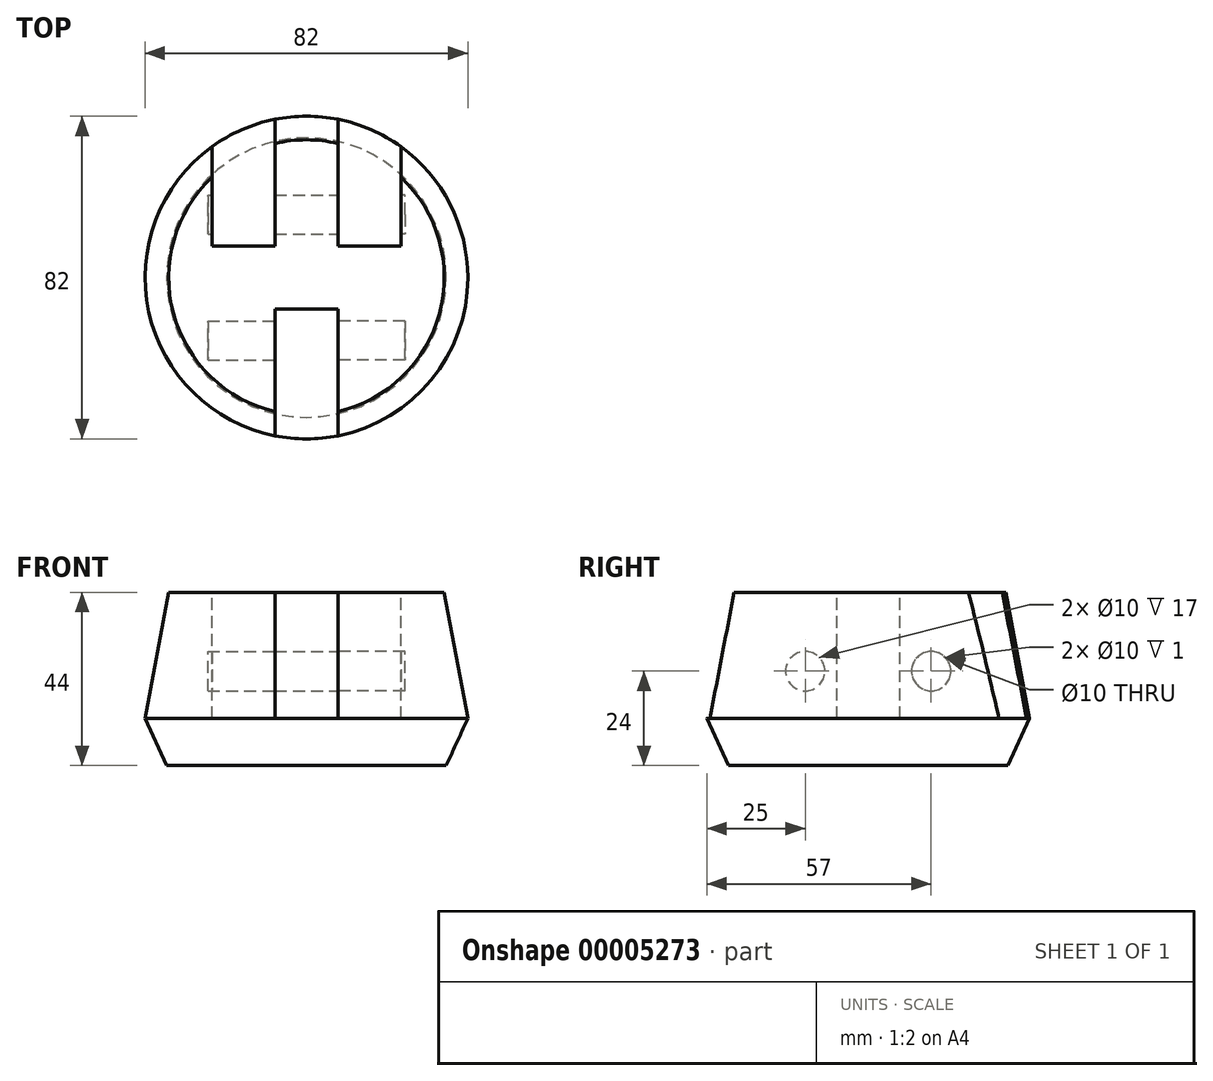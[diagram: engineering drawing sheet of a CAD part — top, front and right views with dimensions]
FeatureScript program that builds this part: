
annotation { "Feature Type Name" : "Feature", "Feature Type Description" : "" }
export const myFeature = defineFeature(function(context is Context, id is Id, definition is map)
    precondition{}
    {
        {
            var Q0;
            Q0=qCreatedBy(makeId("Top.planeOp"),FACE);
            var sketch = newSketch(context, id + "F0", { "sketchPlane" : qUnion([Q0])});
            skCircle(sketch, "E0", {"center": v(0, 0) * mm, "radius": 35.5 * mm});
            skSolve(sketch);
        }
        {
            var Q0;
            Q0=qCreatedBy(makeId("Top.planeOp"),FACE);
            cPlane(context, id + "F1", {"entities" : qUnion([Q0]), "cplaneType" : CPlaneType.OFFSET, "offset" : 12 * mm, "width" : 150 * mm, "height" : 150 * mm});
        }
        {
            var Q0;
            Q0=qCreatedBy(id+"F1.planeOp",FACE);
            cPlane(context, id + "F2", {"entities" : qUnion([Q0]), "cplaneType" : CPlaneType.OFFSET, "offset" : 32 * mm, "width" : 150 * mm, "height" : 150 * mm});
        }
        {
            var Q0;
            Q0=qCreatedBy(id+"F1.planeOp",FACE);
            var sketch = newSketch(context, id + "F3", { "sketchPlane" : qUnion([Q0])});
            skCircle(sketch, "E1", {"center": v(0, 0) * mm, "radius": 41 * mm});
            skSolve(sketch);
        }
        {
            var Q0;
            Q0=qCreatedBy(id+"F2.planeOp",FACE);
            var sketch = newSketch(context, id + "F4", { "sketchPlane" : qUnion([Q0])});
            skCircle(sketch, "E2", {"center": v(0, 0) * mm, "radius": 35 * mm});
            skSolve(sketch);
        }
        {
            var Q0;
            Q0=makeQuery(id+"F0.imprint","IMPRINT",FACE,{"disambiguationData":[TD([[makeQuery(id+"F0.imprint","IMPRINT",EDGE,{"derivedFrom":sQuery(id+"F0.wireOp",EDGE,"E0")}),1.0]])]});
            var Q1;
            Q1=makeQuery(id+"F3.imprint","IMPRINT",FACE,{"disambiguationData":[TD([[makeQuery(id+"F3.imprint","IMPRINT",EDGE,{"derivedFrom":sQuery(id+"F3.wireOp",EDGE,"E1")}),1.0]])]});
            loft(context, id + "F5", {"sheetProfilesArray" : [{ "sheetProfileEntities" : qUnion([Q0]) }, { "sheetProfileEntities" : qUnion([Q1]) }]});
        }
        {
            var Q1;
            Q1=makeQuery(id+"F3.imprint","IMPRINT",FACE,{"disambiguationData":[TD([[makeQuery(id+"F3.imprint","IMPRINT",EDGE,{"derivedFrom":sQuery(id+"F3.wireOp",EDGE,"E1")}),1.0]])]});
            var Q2;
            Q2=makeQuery(id+"F4.imprint","IMPRINT",FACE,{"disambiguationData":[TD([[makeQuery(id+"F4.imprint","IMPRINT",EDGE,{"derivedFrom":sQuery(id+"F4.wireOp",EDGE,"E2")}),1.0]])]});
            loft(context, id + "F6", {"operationType" : NewBodyOperationType.ADD, "sheetProfilesArray" : [{ "sheetProfileEntities" : qUnion([Q1]) }, { "sheetProfileEntities" : qUnion([Q2]) }]});
        }
        {
            var Q0;
            Q0=makeQuery(id+"F6.opLoft","CAP_FACE",FACE,{"disambiguationData":[OSD([makeQuery(id+"F4.imprint","IMPRINT",FACE,{"disambiguationData":[TD([[makeQuery(id+"F4.imprint","IMPRINT",EDGE,{"derivedFrom":sQuery(id+"F4.wireOp",EDGE,"E2")}),1.0]])]})])],"isStart":true});
            var sketch = newSketch(context, id + "F7", { "sketchPlane" : qUnion([Q0])});
            skLineSegment(sketch, "E3.bottom", {"start": v(-8, -48) * mm, "end": v(8, -48) * mm});
            skLineSegment(sketch, "E3.top", {"start": v(-8, -8) * mm, "end": v(8, -8) * mm});
            skLineSegment(sketch, "E3.left", {"start": v(-8, -48) * mm, "end": v(-8, -8) * mm});
            skLineSegment(sketch, "E3.right", {"start": v(8, -48) * mm, "end": v(8, -8) * mm});
            skLineSegment(sketch, "E4.bottom", {"start": v(-24, 48) * mm, "end": v(-8, 48) * mm});
            skLineSegment(sketch, "E4.top", {"start": v(-24, 8) * mm, "end": v(-8, 8) * mm});
            skLineSegment(sketch, "E4.left", {"start": v(-24, 48) * mm, "end": v(-24, 8) * mm});
            skLineSegment(sketch, "E4.right", {"start": v(-8, 48) * mm, "end": v(-8, 8) * mm});
            skLineSegment(sketch, "E5.bottom", {"start": v(8, 48) * mm, "end": v(24, 48) * mm});
            skLineSegment(sketch, "E5.top", {"start": v(8, 8) * mm, "end": v(24, 8) * mm});
            skLineSegment(sketch, "E5.left", {"start": v(8, 48) * mm, "end": v(8, 8) * mm});
            skLineSegment(sketch, "E5.right", {"start": v(24, 48) * mm, "end": v(24, 8) * mm});
            skPoint(sketch, "E6", {"position": v(0, -8) * mm});
            skSolve(sketch);
        }
        {
            var Q0;
            {var subQ6=sQuery(id+"F7.wireOp",EDGE,"E3.bottom");var subQ12=sQuery(id+"F7.wireOp",EDGE,"E4.bottom");var subQ18=sQuery(id+"F7.wireOp",EDGE,"E5.bottom");var subQ19=sQuery(id+"F7.wireOp",EDGE,"E3.top");var subQ20=sQuery(id+"F7.wireOp",EDGE,"E4.top");var subQ21=sQuery(id+"F7.wireOp",EDGE,"E5.top");Q0=qUnion([makeQuery(id+"F7.imprint","IMPRINT",FACE,{"disambiguationData":[TD([[makeQuery(id+"F7.imprint","IMPRINT",EDGE,{"derivedFrom":subQ6}),1.0]])]}),makeQuery(id+"F7.imprint","IMPRINT",FACE,{"disambiguationData":[TD([[makeQuery(id+"F7.imprint","IMPRINT",EDGE,{"derivedFrom":subQ12}),-1.0]])]}),makeQuery(id+"F7.imprint","IMPRINT",FACE,{"disambiguationData":[TD([[makeQuery(id+"F7.imprint","IMPRINT",EDGE,{"derivedFrom":subQ18}),-1.0]])]}),makeQuery(id+"F7.imprint","IMPRINT",FACE,{"disambiguationData":[TD([[makeQuery(id+"F7.imprint","IMPRINT",EDGE,{"derivedFrom":subQ19}),-1.0]])]}),makeQuery(id+"F7.imprint","IMPRINT",FACE,{"disambiguationData":[TD([[makeQuery(id+"F7.imprint","IMPRINT",EDGE,{"derivedFrom":subQ20}),1.0]])]}),makeQuery(id+"F7.imprint","IMPRINT",FACE,{"disambiguationData":[TD([[makeQuery(id+"F7.imprint","IMPRINT",EDGE,{"derivedFrom":subQ21}),1.0]])]})]);}
            extrude(context, id + "F8", {"entities" : qUnion([Q0]), "operationType" : NewBodyOperationType.REMOVE, "oppositeDirection" : true, "depth" : 32 * mm});
        }
        {
            var Q0;
            Q0=qCreatedBy(makeId("Right.planeOp"),FACE);
            var sketch = newSketch(context, id + "F9", { "sketchPlane" : qUnion([Q0])});
            skCircle(sketch, "E7", {"center": v(-16, 24) * mm, "radius": 5 * mm});
            skCircle(sketch, "E8", {"center": v(16, 24) * mm, "radius": 5 * mm});
            skSolve(sketch);
        }
        {
            var Q0;
            {Q0=qUnion([makeQuery(id+"F9.imprint","IMPRINT",FACE,{"disambiguationData":[TD([[makeQuery(id+"F9.imprint","IMPRINT",EDGE,{"derivedFrom":sQuery(id+"F9.wireOp",EDGE,"E7")}),1.0]])]}),makeQuery(id+"F9.imprint","IMPRINT",FACE,{"disambiguationData":[TD([[makeQuery(id+"F9.imprint","IMPRINT",EDGE,{"derivedFrom":sQuery(id+"F9.wireOp",EDGE,"E8")}),1.0]])]})]);}
            extrude(context, id + "F10", {"entities" : qUnion([Q0]), "operationType" : NewBodyOperationType.REMOVE, "oppositeDirection" : true, "depth" : 25 * mm});
        }
        {
            var Q0;
            {Q0=qUnion([makeQuery(id+"F9.imprint","IMPRINT",FACE,{"disambiguationData":[TD([[makeQuery(id+"F9.imprint","IMPRINT",EDGE,{"derivedFrom":sQuery(id+"F9.wireOp",EDGE,"E7")}),1.0]])]}),makeQuery(id+"F9.imprint","IMPRINT",FACE,{"disambiguationData":[TD([[makeQuery(id+"F9.imprint","IMPRINT",EDGE,{"derivedFrom":sQuery(id+"F9.wireOp",EDGE,"E8")}),1.0]])]})]);}
            extrude(context, id + "F11", {"entities" : qUnion([Q0]), "operationType" : NewBodyOperationType.REMOVE, "depth" : 25 * mm});
        }
    });
